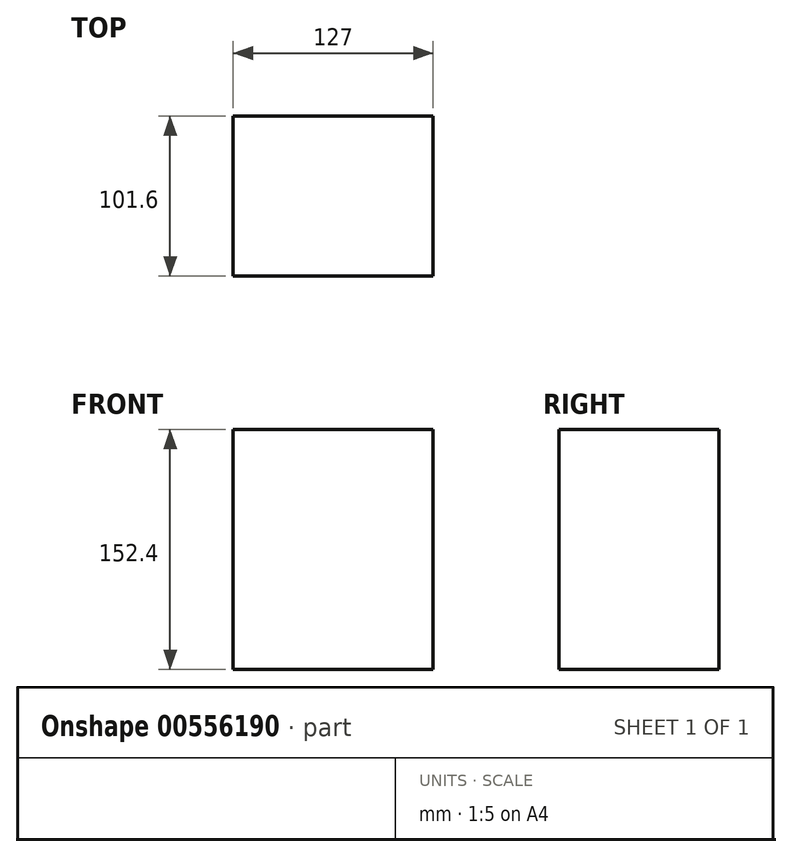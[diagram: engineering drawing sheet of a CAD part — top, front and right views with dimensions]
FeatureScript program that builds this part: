
annotation { "Feature Type Name" : "Feature", "Feature Type Description" : "" }
export const myFeature = defineFeature(function(context is Context, id is Id, definition is map)
    precondition{}
    {
        {
            var Q0;
            Q0=qCreatedBy(makeId("Top.planeOp"),FACE);
            var sketch = newSketch(context, id + "F0", { "sketchPlane" : qUnion([Q0])});
            skLineSegment(sketch, "E0.bottom", {"start": v(-127, 101.6) * mm, "end": v(0, 101.6) * mm});
            skLineSegment(sketch, "E0.top", {"start": v(-127, 0) * mm, "end": v(0, 0) * mm});
            skLineSegment(sketch, "E0.left", {"start": v(-127, 101.6) * mm, "end": v(-127, 0) * mm});
            skLineSegment(sketch, "E0.right", {"start": v(0, 101.6) * mm, "end": v(0, 0) * mm});
            skSolve(sketch);
        }
        {
            var Q0;
            Q0 = qSketchRegion(id + "F0", true);
            extrude(context, id + "F1", {"entities" : qUnion([Q0]), "depth" : 152.4 * mm, "offsetDistance" : 25.4 * mm});
        }
    });
